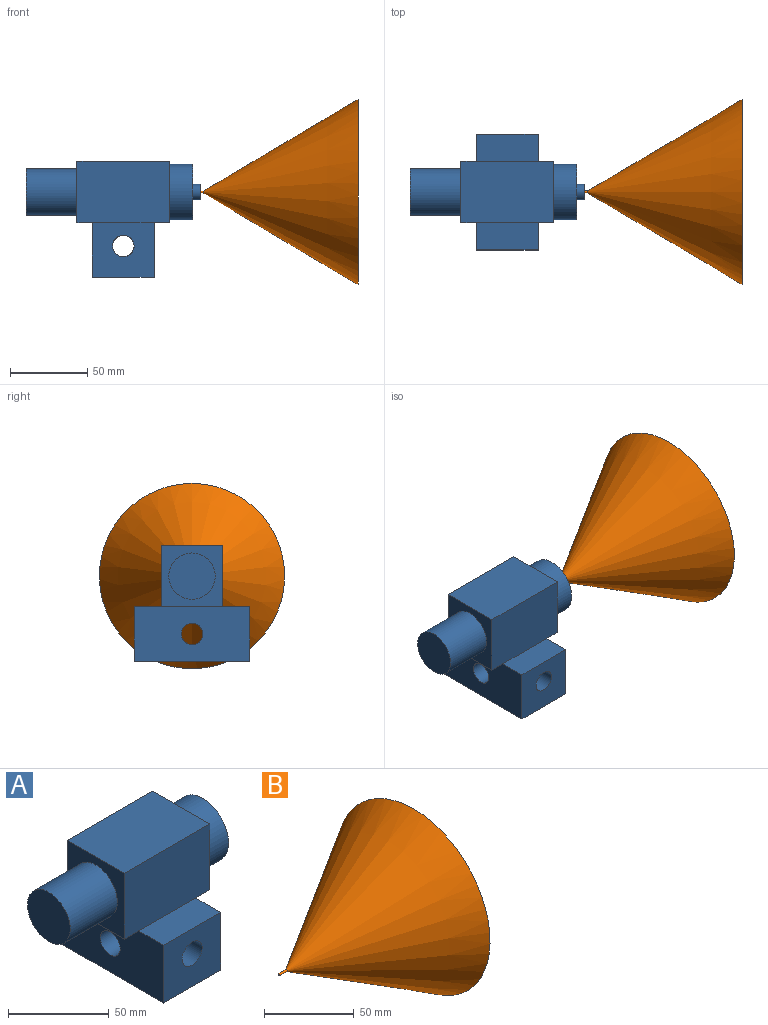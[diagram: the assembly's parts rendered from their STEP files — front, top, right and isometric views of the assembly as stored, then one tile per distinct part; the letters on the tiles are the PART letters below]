
ASSEMBLY  parts=2 mates=1
PART A: 26 faces, bbox 113x75x75 mm
  f0: cylinder r=18mm len=36mm, axis (-1,0,0), area 1696.5mm2, adj f8,f22
  f1: cylinder r=7mm len=75mm, axis (0,-1,0), area 2929mm2, adj f2,f3,f15,f17,f20
  f2: cylinder r=7mm len=19.04mm, axis (-1,0,0), area 642.7mm2, adj f1,f14,f20
  f3: cylinder r=7mm len=19.04mm, axis (-1,0,0), area 642.7mm2, adj f1,f16,f20
  f4: plane 40x10mm, normal (0,0,-1), area 400mm2, adj f8,f9,f10,f14
  f5: plane 60x40mm, normal (0,0,1), area 2400mm2, adj f6,f8,f9,f10
  f6: plane 40x40mm, normal (-1,0,0), area 893.1mm2, adj f5,f7,f9,f10,f11
  f7: plane 40x10mm, normal (0,0,-1), area 400mm2, adj f6,f9,f10,f16
  f8: plane 40x40mm, normal (1,0,0), area 582.1mm2, adj f0,f4,f5,f9,f10
  f9: plane 60x40mm, normal (0,1,0), area 2400mm2, adj f4,f5,f6,f7,f8,f13
  f10: plane 60x40mm, normal (0,-1,0), area 2400mm2, adj f4,f5,f6,f7,f8,f19
  f11: cylinder r=15mm len=33mm, axis (1,0,0), area 3110.2mm2, adj f6,f12
  f12: plane 30x30mm, normal (-1,0,0), area 706.9mm2, adj f11
  f13: plane 40x17.5mm, normal (0,0,1), area 700mm2, adj f9,f14,f16,f17
  f14: plane 75x35mm, normal (1,0,0), area 2471.1mm2, adj f2,f4,f13,f15,f17,f18,f19
  f15: plane 40x35mm, normal (0,-1,0), area 1246.1mm2, adj f1,f14,f16,f18,f19
  f16: plane 75x35mm, normal (-1,0,0), area 2471.1mm2, adj f3,f7,f13,f15,f17,f18,f19
  f17: plane 40x35mm, normal (0,1,0), area 1246.1mm2, adj f1,f13,f14,f16,f18
  f18: plane 75x40mm, normal (0,0,-1), area 2905mm2, adj f14,f15,f16,f17,f20
  f19: plane 40x17.5mm, normal (0,0,1), area 700mm2, adj f10,f14,f15,f16
  f20: cylinder r=5.5mm len=13.07mm, axis (0,0,-1), area 405.9mm2, adj f1,f2,f3,f18
  f21: cylinder r=5mm len=10mm, axis (1,0,0), area 157.1mm2, adj f22,f25
  f22: plane 36x36mm, normal (1,0,0), area 939.3mm2, adj f0,f21
  f23: cone r=0mm half-angle=59deg, axis (1,0,0), area 1.8mm2, adj f24
  f24: cylinder r=0.7mm len=6mm, axis (1,0,0), area 26.4mm2, adj f23,f25
  f25: plane 10x10mm, normal (1,0,0), area 77mm2, adj f21,f24
PART B: 5 faces, bbox 106x120x120 mm
  f0: cylinder r=0.65mm len=6mm, axis (-1,0,0), area 24.5mm2, adj f1,f3
  f1: plane 1.3x1.3mm, normal (-1,0,0), area 1.3mm2, adj f0
  f2: plane 120x120mm, normal (1,0,0), area 859.8mm2, adj f3,f4
  f3: cone r=0.65mm half-angle=30.7deg, axis (1,0,0), area 22156.8mm2, adj f0,f2
  f4: cone r=0.65mm half-angle=30.7deg, axis (1,0,0), area 20474.9mm2, adj f2
PLACE A at identity
PLACE B t=(52,0,20)mm
MATE revolute B.f0 <-> A.f0  axis (1,0,0) through (52,0,20)mm
